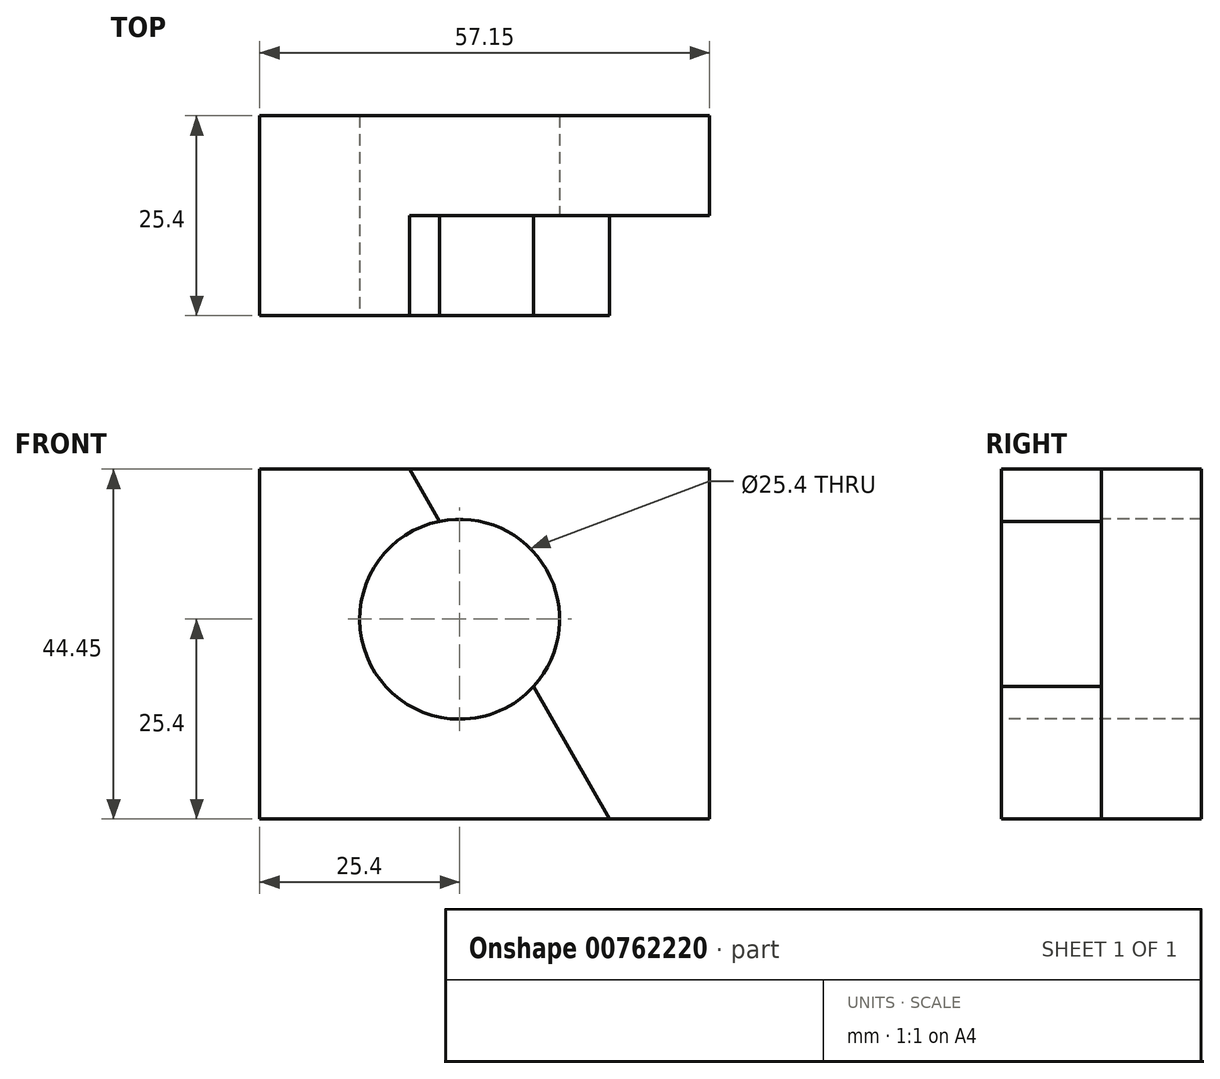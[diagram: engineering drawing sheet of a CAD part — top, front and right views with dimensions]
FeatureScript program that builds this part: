
annotation { "Feature Type Name" : "Feature", "Feature Type Description" : "" }
export const myFeature = defineFeature(function(context is Context, id is Id, definition is map)
    precondition{}
    {
        {
            var Q0;
            Q0=qCreatedBy(makeId("Front.planeOp"),FACE);
            var sketch = newSketch(context, id + "F0", { "sketchPlane" : qUnion([Q0])});
            skLineSegment(sketch, "E0", {"start": v(0, 0) * mm, "end": v(57.15, 0) * mm});
            skLineSegment(sketch, "E1", {"start": v(57.15, 0) * mm, "end": v(57.15, 44.45) * mm});
            skLineSegment(sketch, "E2", {"start": v(57.15, 44.45) * mm, "end": v(0, 44.45) * mm});
            skLineSegment(sketch, "E3", {"start": v(0, 44.45) * mm, "end": v(0, 0) * mm});
            skSolve(sketch);
        }
        {
            var Q0;
            Q0 = qSketchRegion(id + "F0", true);
            extrude(context, id + "F1", {"entities" : qUnion([Q0]), "depth" : 25.4 * mm, "offsetDistance" : 25.4 * mm});
        }
        {
            var Q0;
            Q0=makeQuery(id+"F1.opExtrude","CAP_FACE",FACE,{"disambiguationData":[OSD([sQuery(id+"F0.wireOp",EDGE,"E0"),sQuery(id+"F0.wireOp",EDGE,"E1"),sQuery(id+"F0.wireOp",EDGE,"E2"),sQuery(id+"F0.wireOp",EDGE,"E3")])],"isStart":false});
            var sketch = newSketch(context, id + "F2", { "sketchPlane" : qUnion([Q0])});
            skLineSegment(sketch, "E4", {"start": v(25.4, 44.45) * mm, "end": v(25.4, 0) * mm});
            skLineSegment(sketch, "E5", {"start": v(0, 25.4) * mm, "end": v(57.15, 25.4) * mm});
            skCircle(sketch, "E6", {"center": v(25.4, 25.4) * mm, "radius": 12.7 * mm});
            skSolve(sketch);
        }
        {
            var Q0;
            {var subQ0=sQuery(id+"F2.wireOp",EDGE,"E5");var subQ1=sQuery(id+"F2.wireOp",EDGE,"E4");var subQ2=makeQuery(id+"F2.imprint","INTERSECT",VERTEX,{"derivedFrom":[subQ1,subQ0]});Q0=makeQuery(id+"F2.imprint","IMPRINT",FACE,{"disambiguationData":[TD([[makeQuery(id+"F2.imprint","IMPRINT",EDGE,{"disambiguationData":[TD([[subQ2,-1.0]])],"derivedFrom":subQ1}),-1.0]])]});}
            var Q1;
            {var subQ0=sQuery(id+"F2.wireOp",EDGE,"E6");var subQ1=sQuery(id+"F2.wireOp",EDGE,"E4");var subQ2=makeQuery(id+"F2.imprint","INTERSECT",VERTEX,{"disambiguationData":[OD(0.0)],"derivedFrom":[subQ1,subQ0]});Q1=makeQuery(id+"F2.imprint","IMPRINT",FACE,{"disambiguationData":[TD([[makeQuery(id+"F2.imprint","IMPRINT",EDGE,{"disambiguationData":[TD([[subQ2,-1.0]])],"derivedFrom":subQ1}),-1.0]])]});}
            var Q2;
            {var subQ0=sQuery(id+"F2.wireOp",EDGE,"E6");var subQ1=sQuery(id+"F2.wireOp",EDGE,"E4");var subQ2=makeQuery(id+"F2.imprint","INTERSECT",VERTEX,{"disambiguationData":[OD(0.0)],"derivedFrom":[subQ1,subQ0]});Q2=makeQuery(id+"F2.imprint","IMPRINT",FACE,{"disambiguationData":[TD([[makeQuery(id+"F2.imprint","IMPRINT",EDGE,{"disambiguationData":[TD([[subQ2,-1.0]])],"derivedFrom":subQ1}),1.0]])]});}
            var Q3;
            {var subQ0=sQuery(id+"F2.wireOp",EDGE,"E5");var subQ1=sQuery(id+"F2.wireOp",EDGE,"E4");var subQ2=makeQuery(id+"F2.imprint","INTERSECT",VERTEX,{"derivedFrom":[subQ1,subQ0]});Q3=makeQuery(id+"F2.imprint","IMPRINT",FACE,{"disambiguationData":[TD([[makeQuery(id+"F2.imprint","IMPRINT",EDGE,{"disambiguationData":[TD([[subQ2,-1.0]])],"derivedFrom":subQ1}),1.0]])]});}
            extrude(context, id + "F3", {"entities" : qUnion([Q0, Q1, Q2, Q3]), "operationType" : NewBodyOperationType.REMOVE, "endBound" : BoundingType.THROUGH_ALL, "oppositeDirection" : true, "depth" : 25.4 * mm, "offsetDistance" : 25.4 * mm});
        }
        {
            var Q0;
            Q0=makeQuery(id+"F1.opExtrude","CAP_FACE",FACE,{"disambiguationData":[OSD([sQuery(id+"F0.wireOp",EDGE,"E0"),sQuery(id+"F0.wireOp",EDGE,"E1"),sQuery(id+"F0.wireOp",EDGE,"E2"),sQuery(id+"F0.wireOp",EDGE,"E3")])],"isStart":false});
            var sketch = newSketch(context, id + "F4", { "sketchPlane" : qUnion([Q0])});
            skLineSegment(sketch, "E7", {"start": v(19.05, 44.45) * mm, "end": v(44.45, 0) * mm});
            skSolve(sketch);
        }
        {
            var Q0;
            {var subQ0=makeQuery(id+"F1.opExtrude","CAP_EDGE",EDGE,{"disambiguationData":[OSD([sQuery(id+"F0.wireOp",EDGE,"E1")])],"isStart":false});Q0=makeQuery(id+"F4.imprint","IMPRINT",FACE,{"disambiguationData":[TD([[makeQuery(id+"F4.imprint","IMPRINT",EDGE,{"derivedFrom":subQ0}),1.0]])]});}
            extrude(context, id + "F5", {"entities" : qUnion([Q0]), "operationType" : NewBodyOperationType.REMOVE, "oppositeDirection" : true, "depth" : 12.7 * mm, "offsetDistance" : 25.4 * mm});
        }
    });
